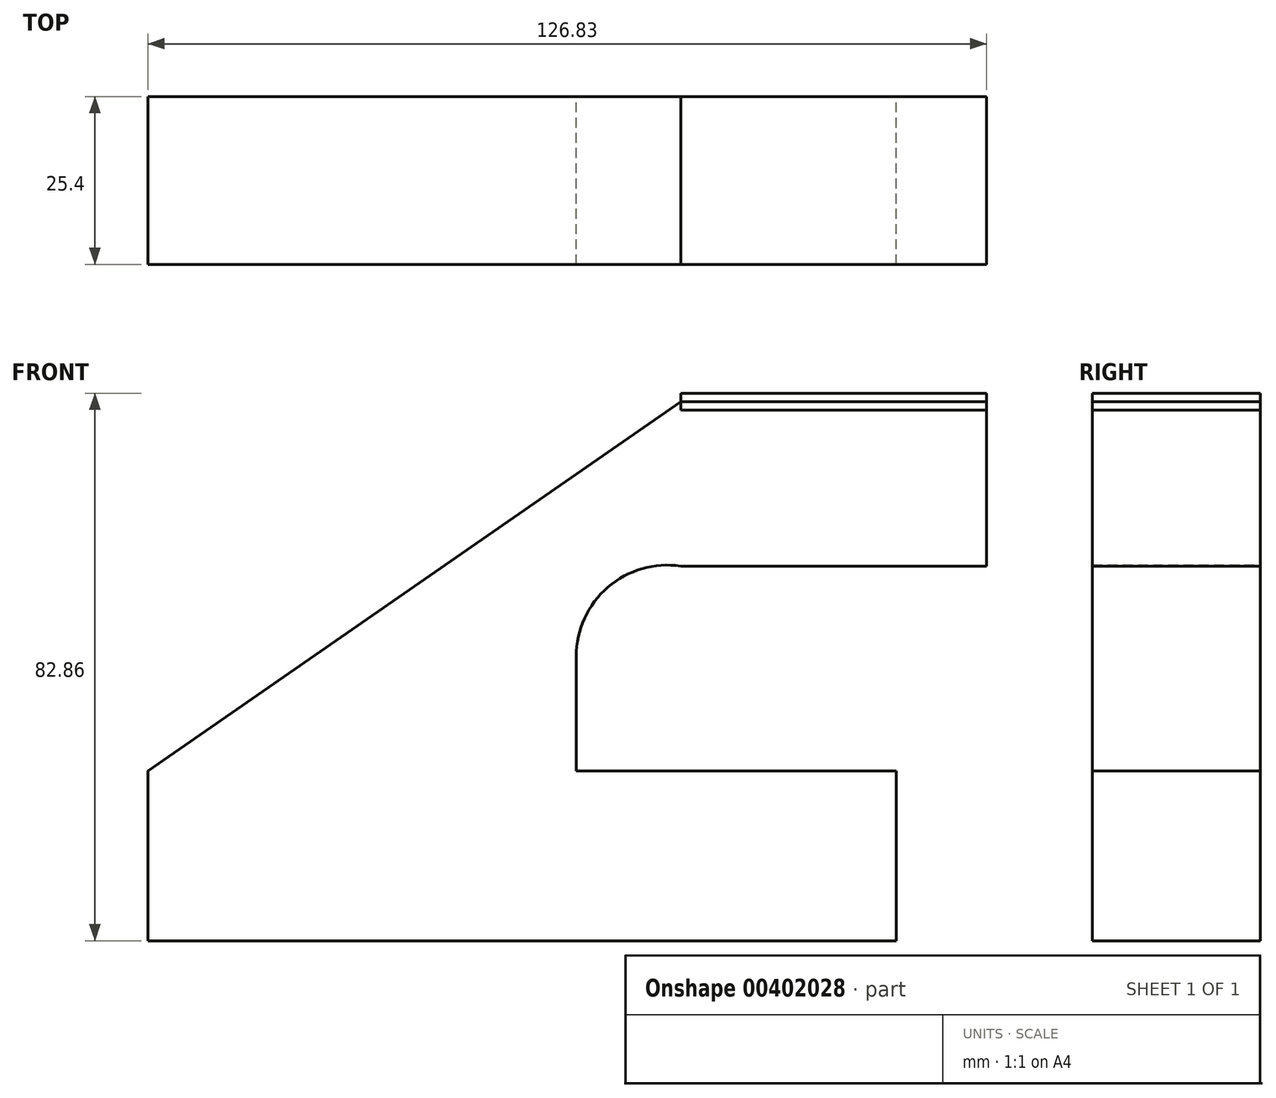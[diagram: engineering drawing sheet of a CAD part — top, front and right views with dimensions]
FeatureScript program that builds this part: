
annotation { "Feature Type Name" : "Feature", "Feature Type Description" : "" }
export const myFeature = defineFeature(function(context is Context, id is Id, definition is map)
    precondition{}
    {
        {
            var Q0;
            Q0=qCreatedBy(makeId("Front.planeOp"),FACE);
            var sketch = newSketch(context, id + "F0", { "sketchPlane" : qUnion([Q0])});
            skLineSegment(sketch, "E0.bottom", {"start": v(-56.6, 12.84) * mm, "end": v(56.6, 12.84) * mm});
            skLineSegment(sketch, "E0.top", {"start": v(-56.6, -12.84) * mm, "end": v(56.6, -12.84) * mm});
            skLineSegment(sketch, "E0.left", {"start": v(-56.6, 12.84) * mm, "end": v(-56.6, -12.84) * mm});
            skLineSegment(sketch, "E0.right", {"start": v(56.6, 12.84) * mm, "end": v(56.6, -12.84) * mm});
            skPoint(sketch, "E0.middle", {"position": v(0, 0) * mm});
            skLineSegment(sketch, "E1.bottom", {"start": v(24, 68.75) * mm, "end": v(70.23, 68.75) * mm});
            skLineSegment(sketch, "E1.top", {"start": v(24, 43.86) * mm, "end": v(70.23, 43.86) * mm});
            skLineSegment(sketch, "E1.left", {"start": v(24, 68.75) * mm, "end": v(24, 43.86) * mm});
            skLineSegment(sketch, "E1.right", {"start": v(70.23, 68.75) * mm, "end": v(70.23, 43.86) * mm});
            skPoint(sketch, "E1.middle", {"position": v(47.12, 56.3) * mm});
            skLineSegment(sketch, "E2", {"start": v(24, 68.75) * mm, "end": v(-56.6, 12.84) * mm});
            skLineSegment(sketch, "E3", {"start": v(8.2, 12.84) * mm, "end": v(8.2, 30.23) * mm});
            skArc(sketch, "E4", {"start": v(8.2, 30.23) * mm, "mid": v(12.98, 40.66) * mm, "end": v(24, 43.86) * mm});
            skSolve(sketch);
        }
        {
            var Q0;
            Q0=makeQuery(id+"F0.imprint","IMPRINT",FACE,{"disambiguationData":[TD([[makeQuery(id+"F0.imprint","IMPRINT",EDGE,{"derivedFrom":sQuery(id+"F0.wireOp",EDGE,"E0.top")}),1.0]])]});
            var Q1;
            Q1=makeQuery(id+"F0.imprint","IMPRINT",FACE,{"disambiguationData":[TD([[makeQuery(id+"F0.imprint","IMPRINT",EDGE,{"derivedFrom":sQuery(id+"F0.wireOp",EDGE,"E1.left")}),-1.0]])]});
            var Q2;
            Q2=makeQuery(id+"F0.imprint","IMPRINT",FACE,{"disambiguationData":[TD([[makeQuery(id+"F0.imprint","IMPRINT",EDGE,{"derivedFrom":sQuery(id+"F0.wireOp",EDGE,"E1.bottom")}),-1.0]])]});
            extrude(context, id + "F1", {"entities" : qUnion([Q0, Q1, Q2]), "endBound" : BoundingType.SYMMETRIC, "depth" : 25.4 * mm});
        }
        {
            var Q0;
            Q0=makeQuery(id+"F1.opExtrude","SWEPT_FACE",FACE,{"disambiguationData":[OSD([sQuery(id+"F0.wireOp",EDGE,"E1.bottom")])]});
            var sketch = newSketch(context, id + "F2", { "sketchPlane" : qUnion([Q0])});
            skSolve(sketch);
        }
        {
            var Q0;
            {var subQ0=sQuery(id+"F0.wireOp",EDGE,"E1.bottom");Q0=makeQuery(id+"F2.imprint","IMPRINT",FACE,{"disambiguationData":[TD([[makeQuery(id+"F2.imprint","IMPRINT",EDGE,{"derivedFrom":makeQuery(id+"F1.opExtrude","CAP_EDGE",EDGE,{"disambiguationData":[OSD([subQ0])],"isStart":true})}),-1.0]])]});}
            extrude(context, id + "F3", {"entities" : qUnion([Q0]), "endBound" : BoundingType.SYMMETRIC, "depth" : 2.54 * mm});
        }
    });
